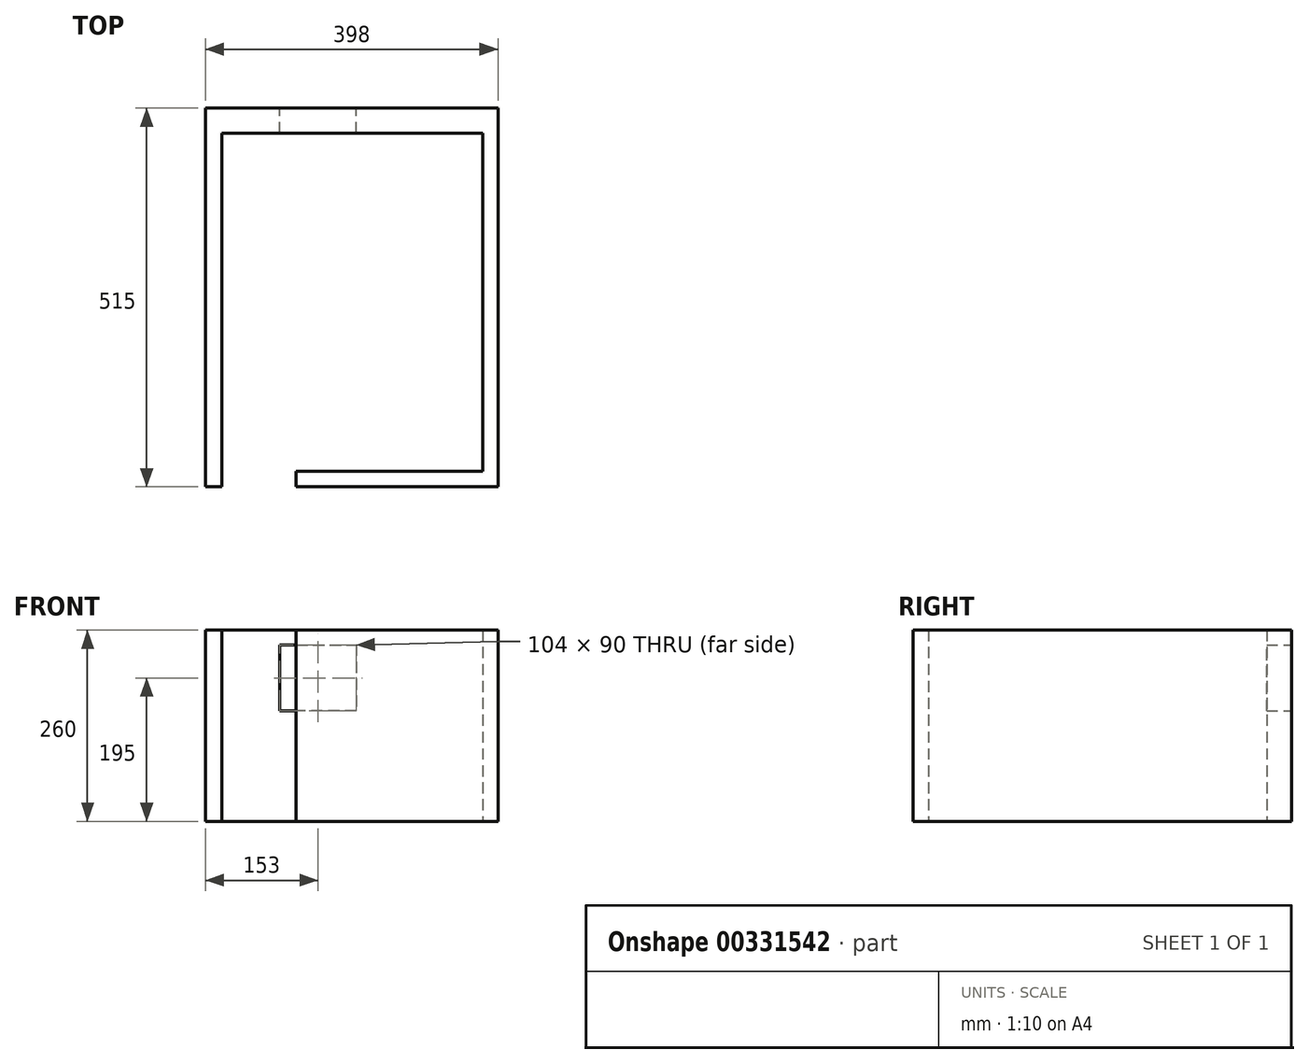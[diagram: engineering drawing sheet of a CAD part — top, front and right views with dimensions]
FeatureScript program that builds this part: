
annotation { "Feature Type Name" : "Feature", "Feature Type Description" : "" }
export const myFeature = defineFeature(function(context is Context, id is Id, definition is map)
    precondition{}
    {
        {
            var Q0;
            Q0=qCreatedBy(makeId("Top.planeOp"),FACE);
            var sketch = newSketch(context, id + "F0", { "sketchPlane" : qUnion([Q0])});
            skLineSegment(sketch, "E0", {"start": v(1313, 440) * mm, "end": v(1313, 406) * mm});
            skLineSegment(sketch, "E1", {"start": v(1313, -267) * mm, "end": v(1313, -301) * mm});
            skLineSegment(sketch, "E2", {"start": v(1313, -301) * mm, "end": v(647, -301) * mm});
            skLineSegment(sketch, "E3", {"start": v(1279, -267) * mm, "end": v(647, -267) * mm});
            skLineSegment(sketch, "E4", {"start": v(1279, 406) * mm, "end": v(688, 406) * mm});
            skLineSegment(sketch, "E5", {"start": v(688, 406) * mm, "end": v(688, -75) * mm});
            skLineSegment(sketch, "E6", {"start": v(688, -75) * mm, "end": v(413, -75) * mm});
            skLineSegment(sketch, "E7", {"start": v(647, -301) * mm, "end": v(647, -267) * mm});
            skLineSegment(sketch, "E8", {"start": v(536, -301) * mm, "end": v(536, -267) * mm});
            skLineSegment(sketch, "E9", {"start": v(536, -267) * mm, "end": v(328, -267) * mm});
            skLineSegment(sketch, "E10", {"start": v(328, -267) * mm, "end": v(328, -407) * mm});
            skLineSegment(sketch, "E11", {"start": v(328, -407) * mm, "end": v(-40, -407) * mm});
            skLineSegment(sketch, "E12", {"start": v(-40, -407) * mm, "end": v(-40, -188) * mm});
            skLineSegment(sketch, "E13", {"start": v(-40, -188) * mm, "end": v(-105, -188) * mm});
            skLineSegment(sketch, "E14", {"start": v(536, -301) * mm, "end": v(362, -301) * mm});
            skLineSegment(sketch, "E15", {"start": v(362, -301) * mm, "end": v(362, -440) * mm});
            skLineSegment(sketch, "E16", {"start": v(-60, -407) * mm, "end": v(-60, -215) * mm});
            skLineSegment(sketch, "E17", {"start": v(-60, -215) * mm, "end": v(-105, -215) * mm});
            skLineSegment(sketch, "E18", {"start": v(-105, -188) * mm, "end": v(-105, -215) * mm});
            skLineSegment(sketch, "E19", {"start": v(-60, -407) * mm, "end": v(-282, -407) * mm});
            skLineSegment(sketch, "E20", {"start": v(-282, -407) * mm, "end": v(-282, -287) * mm});
            skLineSegment(sketch, "E21", {"start": v(-282, -287) * mm, "end": v(-330, -287) * mm});
            skLineSegment(sketch, "E22", {"start": v(-330, -287) * mm, "end": v(-330, -407) * mm});
            skLineSegment(sketch, "E23", {"start": v(-330, -407) * mm, "end": v(-497, -407) * mm});
            skLineSegment(sketch, "E24", {"start": v(-197, -188) * mm, "end": v(-197, -215) * mm});
            skLineSegment(sketch, "E25", {"start": v(-197, -188) * mm, "end": v(-765, -188) * mm});
            skLineSegment(sketch, "E26", {"start": v(-197, -215) * mm, "end": v(-497, -215) * mm});
            skLineSegment(sketch, "E27", {"start": v(-497, -215) * mm, "end": v(-497, -231) * mm});
            skLineSegment(sketch, "E28", {"start": v(-497, -231) * mm, "end": v(-497, -293) * mm});
            skLineSegment(sketch, "E29", {"start": v(-497, -407) * mm, "end": v(-497, -349) * mm});
            skLineSegment(sketch, "E30", {"start": v(413, -75) * mm, "end": v(413, -54) * mm});
            skLineSegment(sketch, "E31", {"start": v(413, -54) * mm, "end": v(667, -54) * mm});
            skLineSegment(sketch, "E32", {"start": v(667, -54) * mm, "end": v(667, 406) * mm});
            skLineSegment(sketch, "E33", {"start": v(667, 406) * mm, "end": v(495, 406) * mm});
            skLineSegment(sketch, "E34", {"start": v(312, 406) * mm, "end": v(391, 406) * mm});
            skLineSegment(sketch, "E35", {"start": v(391, 406) * mm, "end": v(391, 440) * mm});
            skLineSegment(sketch, "E36", {"start": v(495, 406) * mm, "end": v(495, 440) * mm});
            skLineSegment(sketch, "E37", {"start": v(1313, 440) * mm, "end": v(495, 440) * mm});
            skLineSegment(sketch, "E38", {"start": v(312, -75) * mm, "end": v(60, -75) * mm});
            skLineSegment(sketch, "E39", {"start": v(-1279, 406) * mm, "end": v(-1279, 7) * mm});
            skLineSegment(sketch, "E40", {"start": v(-790, 406) * mm, "end": v(-790, 7) * mm});
            skLineSegment(sketch, "E41", {"start": v(-1279, 7) * mm, "end": v(-910, 7) * mm});
            skLineSegment(sketch, "E42", {"start": v(-790, 7) * mm, "end": v(-808, 7) * mm});
            skLineSegment(sketch, "E43", {"start": v(-765, -188) * mm, "end": v(-765, -208) * mm});
            skLineSegment(sketch, "E44", {"start": v(290, 141) * mm, "end": v(290, 406) * mm});
            skLineSegment(sketch, "E45", {"start": v(290, 141) * mm, "end": v(75, 141) * mm});
            skLineSegment(sketch, "E46", {"start": v(75, -46) * mm, "end": v(75, 141) * mm});
            skLineSegment(sketch, "E47", {"start": v(60, -75) * mm, "end": v(60, -46) * mm});
            skLineSegment(sketch, "E48", {"start": v(391, 406) * mm, "end": v(312, 406) * mm});
            skLineSegment(sketch, "E49", {"start": v(-139, 406) * mm, "end": v(-139, 440) * mm});
            skLineSegment(sketch, "E50", {"start": v(-318, 406) * mm, "end": v(-318, 440) * mm});
            skLineSegment(sketch, "E51", {"start": v(-515, 406) * mm, "end": v(-515, 440) * mm});
            skLineSegment(sketch, "E52", {"start": v(-694, 406) * mm, "end": v(-694, 440) * mm});
            skLineSegment(sketch, "E53", {"start": v(-770, 406) * mm, "end": v(-770, 9) * mm});
            skLineSegment(sketch, "E54", {"start": v(-694, 406) * mm, "end": v(-770, 406) * mm});
            skLineSegment(sketch, "E55", {"start": v(75, 406) * mm, "end": v(-139, 406) * mm});
            skLineSegment(sketch, "E56", {"start": v(-318, 406) * mm, "end": v(-515, 406) * mm});
            skLineSegment(sketch, "E57", {"start": v(-318, 440) * mm, "end": v(-515, 440) * mm});
            skLineSegment(sketch, "E58", {"start": v(-770, 9) * mm, "end": v(-754, 9) * mm});
            skLineSegment(sketch, "E59", {"start": v(-677, 9) * mm, "end": v(-659, 9) * mm});
            skLineSegment(sketch, "E60", {"start": v(-659, 9) * mm, "end": v(-659, -5) * mm});
            skLineSegment(sketch, "E61", {"start": v(-659, -5) * mm, "end": v(-659, -46) * mm});
            skLineSegment(sketch, "E62", {"start": v(-659, -46) * mm, "end": v(-60, -46) * mm});
            skLineSegment(sketch, "E63", {"start": v(-60, -75) * mm, "end": v(-60, -46) * mm});
            skLineSegment(sketch, "E64", {"start": v(60, -75) * mm, "end": v(128, -75) * mm});
            skLineSegment(sketch, "E65", {"start": v(60, -46) * mm, "end": v(75, -46) * mm});
            skLineSegment(sketch, "E66", {"start": v(96, -46) * mm, "end": v(290, -46) * mm});
            skLineSegment(sketch, "E67", {"start": v(-60, -75) * mm, "end": v(-677, -75) * mm});
            skLineSegment(sketch, "E68", {"start": v(-677, 9) * mm, "end": v(-677, -75) * mm});
            skLineSegment(sketch, "E69", {"start": v(-754, 9) * mm, "end": v(-754, -13) * mm});
            skLineSegment(sketch, "E70", {"start": v(-808, 7) * mm, "end": v(-808, -13) * mm});
            skLineSegment(sketch, "E71", {"start": v(-808, -13) * mm, "end": v(-754, -13) * mm});
            skLineSegment(sketch, "E72", {"start": v(-910, 7) * mm, "end": v(-910, -29) * mm});
            skLineSegment(sketch, "E73", {"start": v(-1279, -406) * mm, "end": v(-935, -406) * mm});
            skLineSegment(sketch, "E74", {"start": v(-1313, -440) * mm, "end": v(-935, -440) * mm});
            skLineSegment(sketch, "E75", {"start": v(-910, -29) * mm, "end": v(-935, -29) * mm});
            skLineSegment(sketch, "E76", {"start": v(-935, -13) * mm, "end": v(-1279, -13) * mm});
            skLineSegment(sketch, "E77", {"start": v(-910, -132) * mm, "end": v(-935, -132) * mm});
            skLineSegment(sketch, "E78", {"start": v(-910, -29) * mm, "end": v(-910, -13) * mm});
            skLineSegment(sketch, "E79", {"start": v(-935, -406) * mm, "end": v(-935, -132) * mm});
            skLineSegment(sketch, "E80", {"start": v(-935, -29) * mm, "end": v(-935, -13) * mm});
            skLineSegment(sketch, "E81", {"start": v(-877, -208) * mm, "end": v(-877, -188) * mm});
            skLineSegment(sketch, "E82", {"start": v(-910, -132) * mm, "end": v(-910, -188) * mm});
            skLineSegment(sketch, "E83", {"start": v(-877, -188) * mm, "end": v(-910, -188) * mm});
            skLineSegment(sketch, "E84", {"start": v(-877, -208) * mm, "end": v(-904, -208) * mm});
            skLineSegment(sketch, "E85", {"start": v(-904, -208) * mm, "end": v(-904, -406) * mm});
            skLineSegment(sketch, "E86", {"start": v(-904, -406) * mm, "end": v(-648, -406) * mm});
            skLineSegment(sketch, "E87", {"start": v(-765, -208) * mm, "end": v(-648, -208) * mm});
            skLineSegment(sketch, "E88", {"start": v(-648, -208) * mm, "end": v(-648, -273) * mm});
            skLineSegment(sketch, "E89", {"start": v(-648, -406) * mm, "end": v(-648, -343) * mm});
            skLineSegment(sketch, "E90", {"start": v(-935, -440) * mm, "end": v(362, -440) * mm});
            skLineSegment(sketch, "E91", {"start": v(151, 406) * mm, "end": v(151, 440) * mm});
            skLineSegment(sketch, "E92", {"start": v(224, 406) * mm, "end": v(224, 440) * mm});
            skLineSegment(sketch, "E93", {"start": v(290, 406) * mm, "end": v(224, 406) * mm});
            skLineSegment(sketch, "E94", {"start": v(151, 406) * mm, "end": v(96, 406) * mm});
            skLineSegment(sketch, "E95", {"start": v(391, 440) * mm, "end": v(224, 440) * mm});
            skLineSegment(sketch, "E96", {"start": v(151, 440) * mm, "end": v(-139, 440) * mm});
            skLineSegment(sketch, "E97", {"start": v(-907, 406) * mm, "end": v(-907, 440) * mm});
            skLineSegment(sketch, "E98", {"start": v(-1085, 406) * mm, "end": v(-1085, 440) * mm});
            skLineSegment(sketch, "E99", {"start": v(-790, 406) * mm, "end": v(-907, 406) * mm});
            skLineSegment(sketch, "E100", {"start": v(-1085, 406) * mm, "end": v(-1279, 406) * mm});
            skLineSegment(sketch, "E101", {"start": v(-694, 440) * mm, "end": v(-907, 440) * mm});
            skLineSegment(sketch, "E102", {"start": v(-1085, 440) * mm, "end": v(-1313, 440) * mm});
            skLineSegment(sketch, "E103", {"start": v(-1279, -118) * mm, "end": v(-1313, -118) * mm});
            skLineSegment(sketch, "E104", {"start": v(-1279, -297) * mm, "end": v(-1313, -297) * mm});
            skLineSegment(sketch, "E105", {"start": v(-1279, -13) * mm, "end": v(-1279, -118) * mm});
            skLineSegment(sketch, "E106", {"start": v(-1279, -297) * mm, "end": v(-1279, -406) * mm});
            skLineSegment(sketch, "E107", {"start": v(-1313, 440) * mm, "end": v(-1313, -118) * mm});
            skLineSegment(sketch, "E108", {"start": v(-1313, -297) * mm, "end": v(-1313, -440) * mm});
            skLineSegment(sketch, "E109", {"start": v(-648, -273) * mm, "end": v(-630, -273) * mm});
            skLineSegment(sketch, "E110", {"start": v(-648, -343) * mm, "end": v(-630, -343) * mm});
            skLineSegment(sketch, "E111", {"start": v(-515, -349) * mm, "end": v(-497, -349) * mm});
            skLineSegment(sketch, "E112", {"start": v(-515, -293) * mm, "end": v(-497, -293) * mm});
            skLineSegment(sketch, "E113", {"start": v(-515, -349) * mm, "end": v(-515, -406) * mm});
            skLineSegment(sketch, "E114", {"start": v(-630, -343) * mm, "end": v(-630, -406) * mm});
            skLineSegment(sketch, "E115", {"start": v(-630, -406) * mm, "end": v(-515, -406) * mm});
            skLineSegment(sketch, "E116", {"start": v(-630, -273) * mm, "end": v(-630, -206) * mm});
            skLineSegment(sketch, "E117", {"start": v(-630, -206) * mm, "end": v(-515, -206) * mm});
            skLineSegment(sketch, "E118", {"start": v(-515, -293) * mm, "end": v(-515, -206) * mm});
            skLineSegment(sketch, "E119", {"start": v(290, 43) * mm, "end": v(312, 43) * mm});
            skLineSegment(sketch, "E120", {"start": v(290, 124) * mm, "end": v(312, 124) * mm});
            skLineSegment(sketch, "E121", {"start": v(312, -75) * mm, "end": v(312, 43) * mm});
            skLineSegment(sketch, "E122", {"start": v(312, 124) * mm, "end": v(312, 406) * mm});
            skLineSegment(sketch, "E123", {"start": v(290, -46) * mm, "end": v(290, 43) * mm});
            skLineSegment(sketch, "E124", {"start": v(96, 222) * mm, "end": v(75, 222) * mm});
            skLineSegment(sketch, "E125", {"start": v(96, 222) * mm, "end": v(96, 406) * mm});
            skLineSegment(sketch, "E126", {"start": v(75, 222) * mm, "end": v(75, 406) * mm});
            skLineSegment(sketch, "E127", {"start": v(96, -46) * mm, "end": v(96, 124) * mm});
            skLineSegment(sketch, "E128", {"start": v(290, 124) * mm, "end": v(96, 124) * mm});
            skLineSegment(sketch, "E129", {"start": v(1279, -219) * mm, "end": v(1313, -219) * mm});
            skLineSegment(sketch, "E130", {"start": v(1279, -26) * mm, "end": v(1313, -26) * mm});
            skLineSegment(sketch, "E131", {"start": v(1279, 46) * mm, "end": v(1313, 46) * mm});
            skLineSegment(sketch, "E132", {"start": v(1279, 239) * mm, "end": v(1313, 239) * mm});
            skLineSegment(sketch, "E133", {"start": v(1313, 406) * mm, "end": v(1313, 239) * mm});
            skLineSegment(sketch, "E134", {"start": v(1279, 406) * mm, "end": v(1279, 239) * mm});
            skLineSegment(sketch, "E135", {"start": v(1313, 46) * mm, "end": v(1313, -26) * mm});
            skLineSegment(sketch, "E136", {"start": v(1313, -219) * mm, "end": v(1313, -267) * mm});
            skLineSegment(sketch, "E137", {"start": v(1279, 46) * mm, "end": v(1279, -26) * mm});
            skLineSegment(sketch, "E138", {"start": v(1279, -219) * mm, "end": v(1279, -267) * mm});
            skLineSegment(sketch, "E139", {"start": v(1313, -301) * mm, "end": v(1313, 440) * mm});
            skLineSegment(sketch, "E140", {"start": v(1313, -301) * mm, "end": v(362, -301) * mm});
            skLineSegment(sketch, "E141", {"start": v(362, -440) * mm, "end": v(-1313, -440) * mm});
            skLineSegment(sketch, "E142", {"start": v(-1313, 440) * mm, "end": v(-1313, -440) * mm});
            skLineSegment(sketch, "E143", {"start": v(-1313, 440) * mm, "end": v(1313, 440) * mm});
            skLineSegment(sketch, "E144", {"start": v(-321.5, -37.21) * mm, "end": v(-321.5, 162.79) * mm});
            skLineSegment(sketch, "E145", {"start": v(-321.5, -37.21) * mm, "end": v(-511.5, -37.21) * mm});
            skLineSegment(sketch, "E146", {"start": v(-321.5, 162.79) * mm, "end": v(-511.5, 162.79) * mm});
            skLineSegment(sketch, "E147", {"start": v(-511.5, -37.21) * mm, "end": v(-511.5, 162.79) * mm});
            skLineSegment(sketch, "E148", {"start": v(-321.5, -29.2) * mm, "end": v(-511.5, -29.2) * mm});
            skLineSegment(sketch, "E149", {"start": v(-499.08, -21.75) * mm, "end": v(-430.85, -21.75) * mm});
            skLineSegment(sketch, "E150", {"start": v(-430.85, -21.75) * mm, "end": v(-430.85, 2.94) * mm});
            skLineSegment(sketch, "E151", {"start": v(-430.85, 2.94) * mm, "end": v(-499.08, 2.94) * mm});
            skLineSegment(sketch, "E152", {"start": v(-499.08, 2.94) * mm, "end": v(-499.08, -21.75) * mm});
            skLineSegment(sketch, "E153", {"start": v(-333.92, -21.75) * mm, "end": v(-402.15, -21.75) * mm});
            skLineSegment(sketch, "E154", {"start": v(-402.15, -21.75) * mm, "end": v(-402.15, 2.94) * mm});
            skLineSegment(sketch, "E155", {"start": v(-402.15, 2.94) * mm, "end": v(-333.92, 2.94) * mm});
            skLineSegment(sketch, "E156", {"start": v(-333.92, 2.94) * mm, "end": v(-333.92, -21.75) * mm});
            skLineSegment(sketch, "E157", {"start": v(-321.5, 13.1) * mm, "end": v(-416.5, 13.1) * mm});
            skLineSegment(sketch, "E158", {"start": v(-511.5, 36.6) * mm, "end": v(-491.94, 63.04) * mm});
            skLineSegment(sketch, "E159", {"start": v(-491.94, 63.04) * mm, "end": v(-416.5, 13.1) * mm});
            skLineSegment(sketch, "E160", {"start": v(-416.5, 13.1) * mm, "end": v(-511.5, 36.6) * mm});
            skLineSegment(sketch, "E161", {"start": v(-321.5, 159.23) * mm, "end": v(-511.5, 159.23) * mm});
            skLineSegment(sketch, "E162", {"start": v(-552.43, 3.31) * mm, "end": v(-520.43, 3.31) * mm});
            skLineSegment(sketch, "E163", {"start": v(-552.43, 3.31) * mm, "end": v(-552.43, -36.7) * mm});
            skLineSegment(sketch, "E164", {"start": v(-520.43, 3.31) * mm, "end": v(-520.43, -36.7) * mm});
            skLineSegment(sketch, "E165", {"start": v(-552.43, -36.7) * mm, "end": v(-520.43, -36.7) * mm});
            skLineSegment(sketch, "E166", {"start": v(-552.43, -6.69) * mm, "end": v(-520.43, -6.69) * mm});
            skLineSegment(sketch, "E167", {"start": v(-552.43, -3.69) * mm, "end": v(-520.43, -3.69) * mm});
            skLineSegment(sketch, "E168", {"start": v(-552.43, -0.69) * mm, "end": v(-520.43, -0.69) * mm});
            skLineSegment(sketch, "E169", {"start": v(-552.43, 2.31) * mm, "end": v(-520.43, 2.31) * mm});
            skLineSegment(sketch, "E170", {"start": v(-280.57, 3.31) * mm, "end": v(-312.57, 3.31) * mm});
            skLineSegment(sketch, "E171", {"start": v(-280.57, 3.31) * mm, "end": v(-280.57, -36.7) * mm});
            skLineSegment(sketch, "E172", {"start": v(-312.57, 3.31) * mm, "end": v(-312.57, -36.7) * mm});
            skLineSegment(sketch, "E173", {"start": v(-280.57, -36.7) * mm, "end": v(-312.57, -36.7) * mm});
            skLineSegment(sketch, "E174", {"start": v(-280.57, -6.69) * mm, "end": v(-312.57, -6.69) * mm});
            skLineSegment(sketch, "E175", {"start": v(-280.57, -3.69) * mm, "end": v(-312.57, -3.69) * mm});
            skLineSegment(sketch, "E176", {"start": v(-280.57, -0.69) * mm, "end": v(-312.57, -0.69) * mm});
            skLineSegment(sketch, "E177", {"start": v(-280.57, 2.31) * mm, "end": v(-312.57, 2.31) * mm});
            skLineSegment(sketch, "E178", {"start": v(-765, 395.6) * mm, "end": v(-765, 20.6) * mm});
            skLineSegment(sketch, "E179", {"start": v(-765, 395.6) * mm, "end": v(-705, 395.6) * mm});
            skLineSegment(sketch, "E180", {"start": v(-705, 395.6) * mm, "end": v(-705, 20.6) * mm});
            skLineSegment(sketch, "E181", {"start": v(-765, 20.6) * mm, "end": v(-705, 20.6) * mm});
            skLineSegment(sketch, "E182", {"start": v(-705, 395.6) * mm, "end": v(-700, 395.6) * mm});
            skLineSegment(sketch, "E183", {"start": v(-700, 395.6) * mm, "end": v(-700, 20.6) * mm});
            skLineSegment(sketch, "E184", {"start": v(-705, 20.6) * mm, "end": v(-700, 20.6) * mm});
            skLineSegment(sketch, "E185", {"start": v(-705, 114.35) * mm, "end": v(-700, 114.35) * mm});
            skLineSegment(sketch, "E186", {"start": v(-705, 301.85) * mm, "end": v(-700, 301.85) * mm});
            skLineSegment(sketch, "E187", {"start": v(-705, 208.1) * mm, "end": v(-700, 208.1) * mm});
            skLineSegment(sketch, "E188", {"start": v(-705, 348.73) * mm, "end": v(-700, 348.73) * mm});
            skLineSegment(sketch, "E189", {"start": v(-705, 67.47) * mm, "end": v(-700, 67.47) * mm});
            skSolve(sketch);
        }
        {
            var Q0;
            Q0=makeQuery(id+"F0.imprint","IMPRINT",FACE,{"disambiguationData":[TD([[makeQuery(id+"F0.imprint","IMPRINT",EDGE,{"derivedFrom":sQuery(id+"F0.wireOp",EDGE,"E3")}),-1.0]])]});
            var sketch = newSketch(context, id + "F1", { "sketchPlane" : qUnion([Q0])});
            skLineSegment(sketch, "E190.0", {"start": v(688, -75) * mm, "end": v(413, -75) * mm});
            skLineSegment(sketch, "E191.0", {"start": v(290, 141) * mm, "end": v(290, 406) * mm});
            skLineSegment(sketch, "E192.0", {"start": v(290, 440) * mm, "end": v(688, 440) * mm});
            skLineSegment(sketch, "E193.bottom", {"start": v(688, -75) * mm, "end": v(290, -75) * mm});
            skLineSegment(sketch, "E193.top", {"start": v(688, 440) * mm, "end": v(290, 440) * mm});
            skLineSegment(sketch, "E193.left", {"start": v(688, -75) * mm, "end": v(688, 440) * mm});
            skLineSegment(sketch, "E193.right", {"start": v(290, -75) * mm, "end": v(290, 440) * mm});
            skPoint(sketch, "E194.orphan", {"position": v(-1313, 440) * mm});
            skPoint(sketch, "E195.orphan", {"position": v(1313, 440) * mm});
            skSolve(sketch);
        }
        {
            var Q0;
            Q0=qSketchRegion(id+"F1",true);
            extrude(context, id + "F2", {"entities" : qUnion([Q0]), "depth" : 20 * mm});
        }
        {
            var Q0;
            Q0=makeQuery(id+"F2.opExtrude","CAP_FACE",FACE,{"disambiguationData":[OSD([sQuery(id+"F1.wireOp",EDGE,"E193.bottom"),sQuery(id+"F1.wireOp",EDGE,"E193.top"),sQuery(id+"F1.wireOp",EDGE,"E193.left"),sQuery(id+"F1.wireOp",EDGE,"E193.right")])],"isStart":false});
            var sketch = newSketch(context, id + "F3", { "sketchPlane" : qUnion([Q0])});
            skLineSegment(sketch, "E196.0", {"start": v(667, -54) * mm, "end": v(667, 406) * mm});
            skLineSegment(sketch, "E197.0", {"start": v(413, -54) * mm, "end": v(667, -54) * mm});
            skLineSegment(sketch, "E198.0", {"start": v(688, -75) * mm, "end": v(413, -75) * mm});
            skLineSegment(sketch, "E199.0", {"start": v(688, 406) * mm, "end": v(688, -75) * mm});
            skLineSegment(sketch, "E200.0", {"start": v(413, -75) * mm, "end": v(413, -54) * mm});
            skLineSegment(sketch, "E201.0", {"start": v(312, -75) * mm, "end": v(312, 43) * mm});
            skLineSegment(sketch, "E202.0", {"start": v(312, 124) * mm, "end": v(312, 406) * mm});
            skLineSegment(sketch, "E203.0", {"start": v(290, -75) * mm, "end": v(290, 440) * mm});
            skLineSegment(sketch, "E204.0", {"start": v(-1313, 440) * mm, "end": v(1313, 440) * mm});
            skLineSegment(sketch, "E205", {"start": v(312, 43) * mm, "end": v(312, 124) * mm});
            skLineSegment(sketch, "E206", {"start": v(312, 406) * mm, "end": v(667, 406) * mm});
            skLineSegment(sketch, "E207", {"start": v(688, 440) * mm, "end": v(688, 406) * mm});
            skLineSegment(sketch, "E208", {"start": v(290, -75) * mm, "end": v(312, -75) * mm});
            skSolve(sketch);
        }
        {
            var Q0;
            Q0=qSketchRegion(id+"F3",true);
            extrude(context, id + "F4", {"entities" : qUnion([Q0]), "operationType" : NewBodyOperationType.ADD, "depth" : 220 * mm});
        }
        {
            var Q0;
            Q0=makeQuery(id+"F4.boolean.opBoolean","MERGE",FACE,{"derivedFrom":[makeQuery(id+"F2.opExtrude","SWEPT_FACE",FACE,{"disambiguationData":[OSD([sQuery(id+"F1.wireOp",EDGE,"E193.top")])]}),makeQuery(id+"F4.opExtrude","SWEPT_FACE",FACE,{"disambiguationData":[OSD([sQuery(id+"F3.wireOp",EDGE,"E204.0")])]})]});
            var sketch = newSketch(context, id + "F5", { "sketchPlane" : qUnion([Q0])});
            skLineSegment(sketch, "E209.0", {"start": v(-312, 0) * mm, "end": v(-391, 0) * mm, "construction": true});
            skLineSegment(sketch, "E210.0", {"start": v(-667, 0) * mm, "end": v(-495, 0) * mm, "construction": true});
            skLineSegment(sketch, "E211", {"start": v(-391, 220) * mm, "end": v(-495, 220) * mm});
            skLineSegment(sketch, "E212", {"start": v(-495, 220) * mm, "end": v(-495, 130) * mm});
            skLineSegment(sketch, "E213", {"start": v(-495, 130) * mm, "end": v(-391, 130) * mm});
            skLineSegment(sketch, "E214", {"start": v(-391, 130) * mm, "end": v(-391, 220) * mm});
            skSolve(sketch);
        }
        {
            var Q0;
            Q0=qSketchRegion(id+"F5",true);
            extrude(context, id + "F6", {"entities" : qUnion([Q0]), "operationType" : NewBodyOperationType.REMOVE, "oppositeDirection" : true, "depth" : 40 * mm});
        }
        {
            var Q0;
            Q0=makeQuery(id+"F2.opExtrude","CAP_FACE",FACE,{"disambiguationData":[OSD([sQuery(id+"F1.wireOp",EDGE,"E193.bottom"),sQuery(id+"F1.wireOp",EDGE,"E193.top"),sQuery(id+"F1.wireOp",EDGE,"E193.left"),sQuery(id+"F1.wireOp",EDGE,"E193.right")])],"isStart":false});
            extrude(context, id + "F7", {"entities" : qUnion([Q0]), "operationType" : NewBodyOperationType.REMOVE, "oppositeDirection" : true, "depth" : 25 * mm});
        }
        {
            var Q0;
            Q0=makeQuery(id+"F2.opExtrude","CAP_FACE",FACE,{"disambiguationData":[OSD([sQuery(id+"F1.wireOp",EDGE,"E193.bottom"),sQuery(id+"F1.wireOp",EDGE,"E193.top"),sQuery(id+"F1.wireOp",EDGE,"E193.left"),sQuery(id+"F1.wireOp",EDGE,"E193.right")])],"isStart":true});
            extrude(context, id + "F8", {"entities" : qUnion([Q0]), "operationType" : NewBodyOperationType.ADD, "depth" : 20 * mm});
        }
    });
